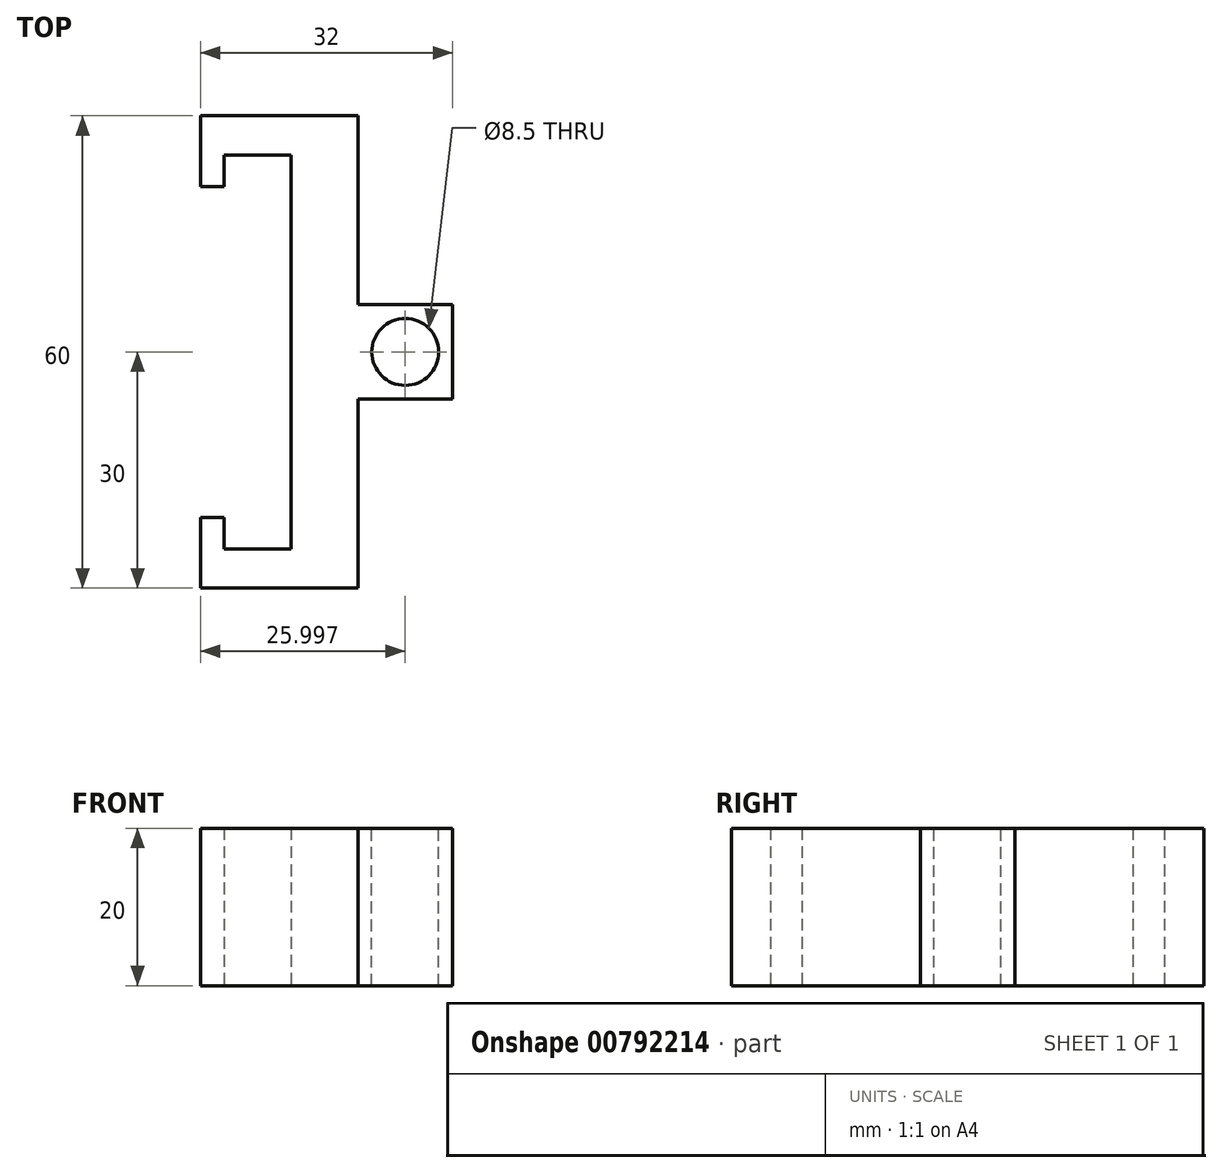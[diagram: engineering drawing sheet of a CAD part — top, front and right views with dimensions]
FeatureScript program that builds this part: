
annotation { "Feature Type Name" : "Feature", "Feature Type Description" : "" }
export const myFeature = defineFeature(function(context is Context, id is Id, definition is map)
    precondition{}
    {
        {
            var Q0;
            Q0=qCreatedBy(makeId("Top.planeOp"),FACE);
            var sketch = newSketch(context, id + "F0", { "sketchPlane" : qUnion([Q0])});
            skLineSegment(sketch, "E0.bottom", {"start": v(0.26, 63.03) * mm, "end": v(20.26, 63.03) * mm});
            skLineSegment(sketch, "E0.top", {"start": v(0.26, 3.03) * mm, "end": v(20.26, 3.03) * mm});
            skLineSegment(sketch, "E1.bottom", {"start": v(20.26, 39.03) * mm, "end": v(32.26, 39.03) * mm});
            skLineSegment(sketch, "E1.top", {"start": v(20.26, 27.03) * mm, "end": v(32.26, 27.03) * mm});
            skLineSegment(sketch, "E1.right", {"start": v(32.26, 39.03) * mm, "end": v(32.26, 27.03) * mm});
            skLineSegment(sketch, "E2.bottom", {"start": v(0.26, 63.03) * mm, "end": v(3.26, 63.03) * mm});
            skLineSegment(sketch, "E2.top", {"start": v(0.26, 54.03) * mm, "end": v(3.26, 54.03) * mm});
            skLineSegment(sketch, "E2.left", {"start": v(0.26, 63.03) * mm, "end": v(0.26, 54.03) * mm});
            skLineSegment(sketch, "E3.bottom", {"start": v(0.26, 3.03) * mm, "end": v(3.26, 3.03) * mm});
            skLineSegment(sketch, "E3.top", {"start": v(0.26, 12.03) * mm, "end": v(3.26, 12.03) * mm});
            skLineSegment(sketch, "E3.left", {"start": v(0.26, 3.03) * mm, "end": v(0.26, 12.03) * mm});
            skLineSegment(sketch, "E4", {"start": v(3.26, 8.03) * mm, "end": v(11.76, 8.03) * mm});
            skLineSegment(sketch, "E5", {"start": v(3.26, 58.03) * mm, "end": v(11.76, 58.03) * mm});
            skLineSegment(sketch, "E6", {"start": v(11.76, 8.03) * mm, "end": v(11.76, 58.03) * mm});
            skLineSegment(sketch, "E7", {"start": v(3.26, 12.03) * mm, "end": v(3.26, 8.03) * mm});
            skLineSegment(sketch, "E8", {"start": v(3.26, 54.03) * mm, "end": v(3.26, 58.03) * mm});
            skLineSegment(sketch, "E9", {"start": v(3.26, 54.03) * mm, "end": v(0.26, 54.03) * mm});
            skLineSegment(sketch, "E10", {"start": v(0.26, 54.03) * mm, "end": v(0.26, 63.03) * mm});
            skLineSegment(sketch, "E11", {"start": v(20.26, 3.03) * mm, "end": v(0.26, 3.03) * mm});
            skLineSegment(sketch, "E12", {"start": v(20.26, 39.03) * mm, "end": v(20.26, 63.03) * mm});
            skLineSegment(sketch, "E13", {"start": v(20.26, 27.03) * mm, "end": v(20.26, 3.03) * mm});
            skLineSegment(sketch, "E14", {"start": v(32.26, 27.03) * mm, "end": v(20.26, 27.03) * mm});
            skSolve(sketch);
        }
        {
            var Q0;
            Q0=qSketchRegion(id+"F0",true);
            extrude(context, id + "F1", {"entities" : qUnion([Q0]), "depth" : 20 * mm, "offsetDistance" : 25 * mm});
        }
        {
            var Q0;
            Q0=makeQuery(id+"F1.opExtrude","CAP_FACE",FACE,{"disambiguationData":[OSD([sQuery(id+"F0.wireOp",EDGE,"E1.right"),sQuery(id+"F0.wireOp",EDGE,"E4"),sQuery(id+"F0.wireOp",EDGE,"E5"),sQuery(id+"F0.wireOp",EDGE,"E6"),sQuery(id+"F0.wireOp",EDGE,"E8"),sQuery(id+"F0.wireOp",EDGE,"E9"),sQuery(id+"F0.wireOp",EDGE,"E10"),sQuery(id+"F0.wireOp",EDGE,"E0.bottom"),sQuery(id+"F0.wireOp",EDGE,"E11"),sQuery(id+"F0.wireOp",EDGE,"E3.left"),sQuery(id+"F0.wireOp",EDGE,"E3.top"),sQuery(id+"F0.wireOp",EDGE,"E7"),sQuery(id+"F0.wireOp",EDGE,"E12"),sQuery(id+"F0.wireOp",EDGE,"E13"),sQuery(id+"F0.wireOp",EDGE,"E1.bottom"),sQuery(id+"F0.wireOp",EDGE,"E14")])],"isStart":false});
            var sketch = newSketch(context, id + "F2", { "sketchPlane" : qUnion([Q0])});
            skCircle(sketch, "E15", {"center": v(26.26, 33.03) * mm, "radius": 4.25 * mm});
            skSolve(sketch);
        }
        {
            var Q0;
            Q0=qSketchRegion(id+"F2",true);
            extrude(context, id + "F3", {"entities" : qUnion([Q0]), "operationType" : NewBodyOperationType.REMOVE, "oppositeDirection" : true, "depth" : 20 * mm, "offsetDistance" : 25 * mm});
        }
    });
